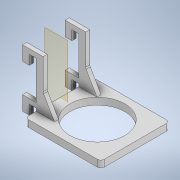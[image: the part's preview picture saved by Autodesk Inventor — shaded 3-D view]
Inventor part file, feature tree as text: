
AUTODESK INVENTOR PART (.ipt)
format: ipt  version: 2021 (Build 250183000, 183)  size: 210,432 bytes
history: native  units: in
note: dims shown in document units (in); Inventor stores cm internally (conversion verified against a paired STEP export)
features: extrude x4, sketch x4, mirror x2, fillet x2, plane x1
ambient origin geometry x8: Origin, YZ Plane, XZ Plane, XY Plane, X Axis, Y Axis, Z Axis, Center Point
bodies: Solid1 (feature_tree)
feature tree (13):
  extrude  "Extrusion1"  Depth=0.175in
  plane  "Work Plane1"
  mirror  "Mirror1"
  extrude  "Extrusion4"  Depth=0.25in
  sketch  "Sketch5"  dims[d7=0.25in d11=0.15in d12=0.0in]
  fillet  "Fillet1"  Radius=0.25in
  extrude  "Extrusion6"  Depth=0.15in TaperAngle=0.0deg
  extrude  "Extrusion7"  Depth=0.525in
  mirror  "Mirror2"
  fillet  "Fillet2"  Radius=0.775in
  sketch  "Sketch1"  dims[d1=1.4in d2=0.175in]
  sketch  "Sketch4"  dims[d3=0.175in d4=0.25in d6=0.25in]
  sketch  "Sketch6"  dims[d13=0.525in d14=0.525in d15=0.775in d23=2.75in d24=0.25in d25=2.5in d26=0.0in d30=0.125in d32=2.0in d33=1.85in d34=0.0in d35=0.4in d36=0.4593in d37=120.0deg d38=0.15in d39=0.0in d40=0.125in]
